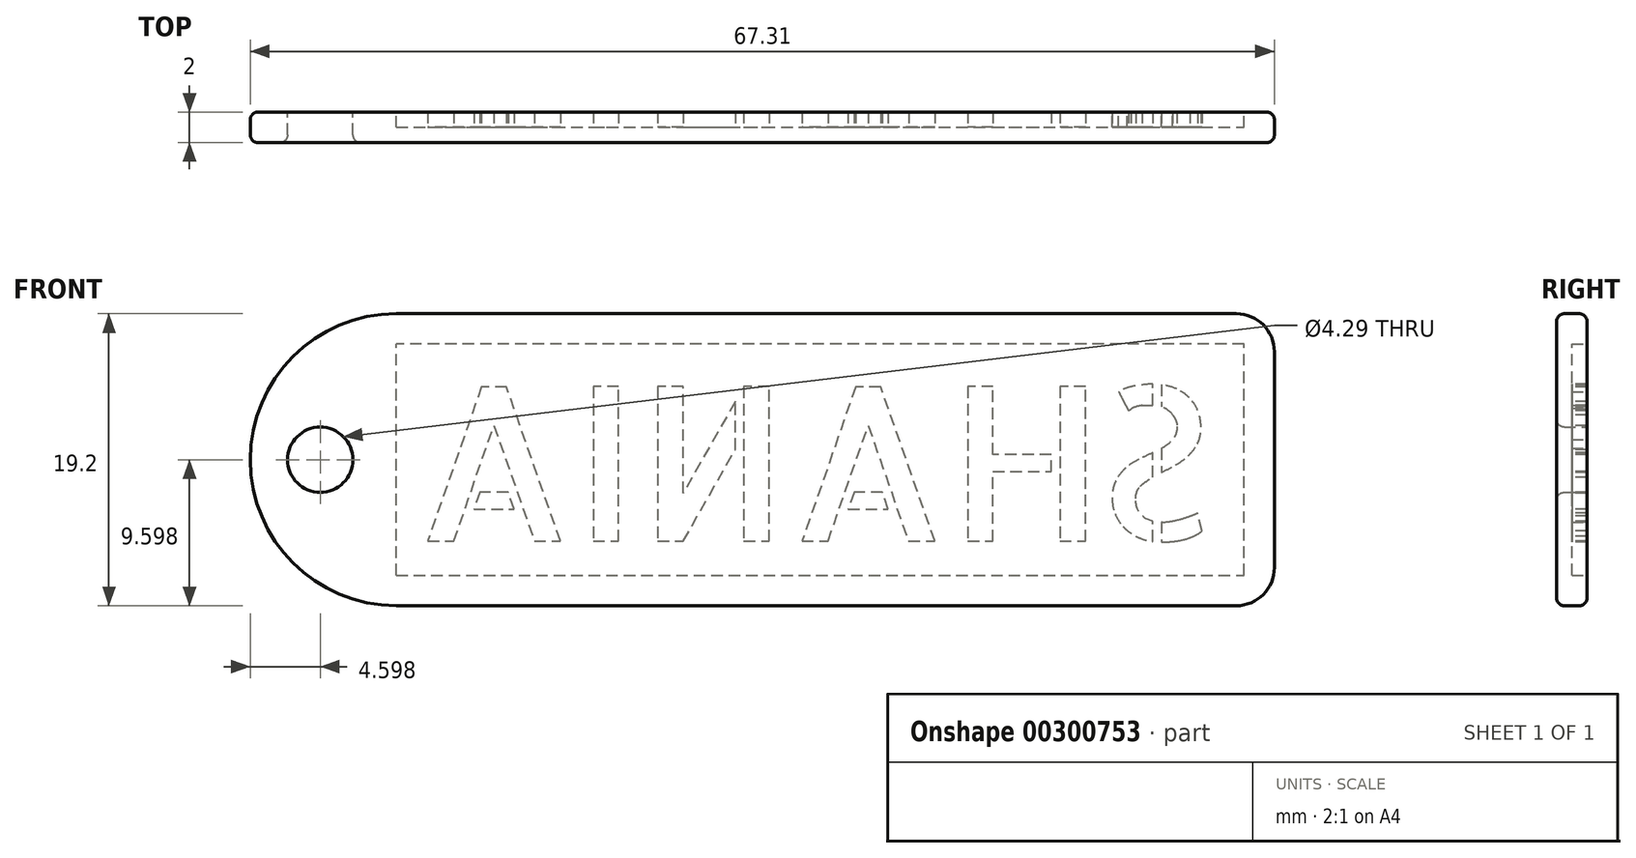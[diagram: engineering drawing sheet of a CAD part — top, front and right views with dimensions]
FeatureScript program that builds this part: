
annotation { "Feature Type Name" : "Feature", "Feature Type Description" : "" }
export const myFeature = defineFeature(function(context is Context, id is Id, definition is map)
    precondition{}
    {
        {
            var Q0;
            Q0=qCreatedBy(makeId("Front.planeOp"),FACE);
            var sketch = newSketch(context, id + "F0", { "sketchPlane" : qUnion([Q0])});
            skLineSegment(sketch, "E0", {"start": v(-2.5, 0) * mm, "end": v(-57.71, 0) * mm});
            skLineSegment(sketch, "E1", {"start": v(-57.71, 19.2) * mm, "end": v(-2.5, 19.2) * mm});
            skLineSegment(sketch, "E2", {"start": v(0, 16.7) * mm, "end": v(0, 2.5) * mm});
            skArc(sketch, "E3", {"start": v(-57.71, 19.2) * mm, "mid": v(-67.3, 9.6) * mm, "end": v(-57.71, 0) * mm});
            skPoint(sketch, "E4.visualSharp", {"position": v(0, 19.2) * mm});
            skArc(sketch, "E4.filletArc", {"start": v(0, 16.7) * mm, "mid": v(-0.73, 18.46) * mm, "end": v(-2.5, 19.2) * mm});
            skPoint(sketch, "E5.visualSharp", {"position": v(0, 0) * mm});
            skArc(sketch, "E5.filletArc", {"start": v(-2.5, 0) * mm, "mid": v(-0.73, 0.73) * mm, "end": v(0, 2.5) * mm});
            skCircle(sketch, "E6", {"center": v(-62.71, 9.6) * mm, "radius": 2.14 * mm});
            skSolve(sketch);
        }
        {
            var Q0;
            Q0=makeQuery(id+"F0.imprint","IMPRINT",FACE,{"disambiguationData":[TD([[makeQuery(id+"F0.imprint","IMPRINT",EDGE,{"derivedFrom":sQuery(id+"F0.wireOp",EDGE,"E0")}),-1.0]])]});
            var sketch = newSketch(context, id + "F1", { "sketchPlane" : qUnion([Q0])});
            skLineSegment(sketch, "E7.0", {"start": v(-2, 2) * mm, "end": v(-2, 17.2) * mm});
            skLineSegment(sketch, "E7.1", {"start": v(-57.71, 2) * mm, "end": v(-2, 2) * mm});
            skArc(sketch, "E7.2", {"start": v(-57.71, 17.2) * mm, "mid": v(-65.3, 9.6) * mm, "end": v(-57.71, 2) * mm});
            skLineSegment(sketch, "E7.3", {"start": v(-2, 17.2) * mm, "end": v(-57.71, 17.2) * mm});
            skSolve(sketch);
        }
        {
            var Q0;
            Q0=makeQuery(id+"F0.imprint","IMPRINT",FACE,{"disambiguationData":[TD([[makeQuery(id+"F0.imprint","IMPRINT",EDGE,{"derivedFrom":sQuery(id+"F0.wireOp",EDGE,"E0")}),-1.0]])]});
            extrude(context, id + "F2", {"entities" : qUnion([Q0]), "depth" : 2 * mm});
        }
        {
            var Q0;
            Q0=makeQuery(id+"F1.imprint","IMPRINT",FACE,{"disambiguationData":[TD([[makeQuery(id+"F1.imprint","IMPRINT",EDGE,{"derivedFrom":sQuery(id+"F1.wireOp",EDGE,"E7.0")}),1.0]])]});
            extrude(context, id + "F3", {"entities" : qUnion([Q0]), "operationType" : NewBodyOperationType.REMOVE, "depth" : 1 * mm});
        }
        {
            var Q0;
            Q0=makeQuery(id+"F3.boolean.opBoolean","COPY",FACE,{"derivedFrom":makeQuery(id+"F3.opExtrude","CAP_FACE",FACE,{"disambiguationData":[OSD([sQuery(id+"F1.wireOp",EDGE,"E7.0"),sQuery(id+"F1.wireOp",EDGE,"E7.1"),sQuery(id+"F1.wireOp",EDGE,"E7.2"),sQuery(id+"F1.wireOp",EDGE,"E7.3")])],"isStart":false})});
            var sketch = newSketch(context, id + "F4", { "sketchPlane" : qUnion([Q0])});
            skLineSegment(sketch, "E8", {"start": v(57.71, 2) * mm, "end": v(57.71, 17.2) * mm});
            skSolve(sketch);
        }
        {
            var Q0;
            Q0=makeQuery(id+"F4.imprint","IMPRINT",FACE,{"disambiguationData":[TD([[makeQuery(id+"F4.imprint","IMPRINT",EDGE,{"derivedFrom":sQuery(id+"F4.wireOp",EDGE,"E8")}),-1.0]])]});
            extrude(context, id + "F5", {"entities" : qUnion([Q0]), "operationType" : NewBodyOperationType.ADD, "depth" : 1 * mm});
        }
        {
            var Q0;
            Q0=makeQuery(id+"F3.boolean.opBoolean","COPY",FACE,{"derivedFrom":makeQuery(id+"F3.opExtrude","CAP_FACE",FACE,{"disambiguationData":[OSD([sQuery(id+"F1.wireOp",EDGE,"E7.0"),sQuery(id+"F1.wireOp",EDGE,"E7.1"),sQuery(id+"F1.wireOp",EDGE,"E7.2"),sQuery(id+"F1.wireOp",EDGE,"E7.3")])],"isStart":false})});
            var sketch = newSketch(context, id + "F6", { "sketchPlane" : qUnion([Q0])});
            skText(sketch, "E9", { "text": "SHANIA", "fontName": "AllertaStencil-Regular.ttf"});
            const initialGuessF6  = {"E9": [0.00364, 0.00424, 1, 0, 0.01017]};
            skSetInitialGuess(sketch, initialGuessF6);
            skSolve(sketch);
        }
        {
            var Q0;
            Q0 = qSketchRegion(id + "F6", true);
            extrude(context, id + "F7", {"entities" : qUnion([Q0]), "operationType" : NewBodyOperationType.ADD, "depth" : 1 * mm});
        }
        {
            var Q0;
            Q0=makeQuery(id+"F2.opExtrude","CAP_EDGE",EDGE,{"disambiguationData":[OSD([sQuery(id+"F0.wireOp",EDGE,"E3")])],"isStart":true});
            var Q1;
            Q1=makeQuery(id+"F2.opExtrude","CAP_EDGE",EDGE,{"disambiguationData":[OSD([sQuery(id+"F0.wireOp",EDGE,"E3")])],"isStart":false});
            var Q2;
            Q2=makeQuery(id+"F2.opExtrude","CAP_FACE",FACE,{"disambiguationData":[OSD([sQuery(id+"F0.wireOp",EDGE,"E0"),sQuery(id+"F0.wireOp",EDGE,"E1"),sQuery(id+"F0.wireOp",EDGE,"E2"),sQuery(id+"F0.wireOp",EDGE,"E3"),sQuery(id+"F0.wireOp",EDGE,"E4.filletArc"),sQuery(id+"F0.wireOp",EDGE,"E5.filletArc"),sQuery(id+"F0.wireOp",EDGE,"E6")])],"isStart":false});
            fillet(context, id + "F8", {"entities" : qUnion([Q0, Q1, Q2]), "radius" : 0.5 * mm, "tangentPropagation" : true, "allowEdgeOverflow" : false});
        }
    });
